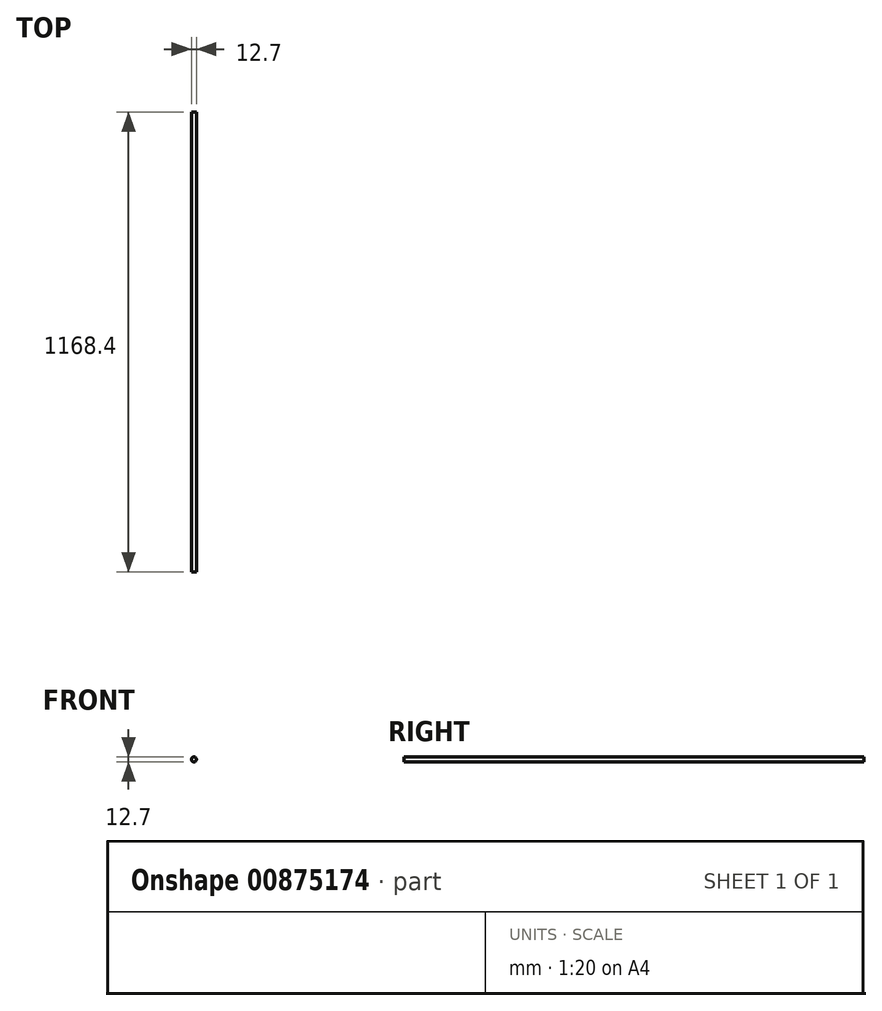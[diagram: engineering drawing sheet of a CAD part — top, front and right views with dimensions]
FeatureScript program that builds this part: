
annotation { "Feature Type Name" : "Feature", "Feature Type Description" : "" }
export const myFeature = defineFeature(function(context is Context, id is Id, definition is map)
    precondition{}
    {
        {
            var Q0;
            Q0=qCreatedBy(makeId("Front.planeOp"),FACE);
            var sketch = newSketch(context, id + "F0", { "sketchPlane" : qUnion([Q0])});
            skCircle(sketch, "E0", {"center": v(-103.38, 20.11) * mm, "radius": 6.35 * mm});
            skSolve(sketch);
        }
        {
            var Q0;
            Q0=makeQuery(id+"F0.imprint","IMPRINT",FACE,{"disambiguationData":[TD([[makeQuery(id+"F0.imprint","IMPRINT",EDGE,{"derivedFrom":sQuery(id+"F0.wireOp",EDGE,"E0")}),1.0]])]});
            extrude(context, id + "F1", {"entities" : qUnion([Q0]), "depth" : 1168.4 * mm, "offsetDistance" : 25.4 * mm});
        }
    });
